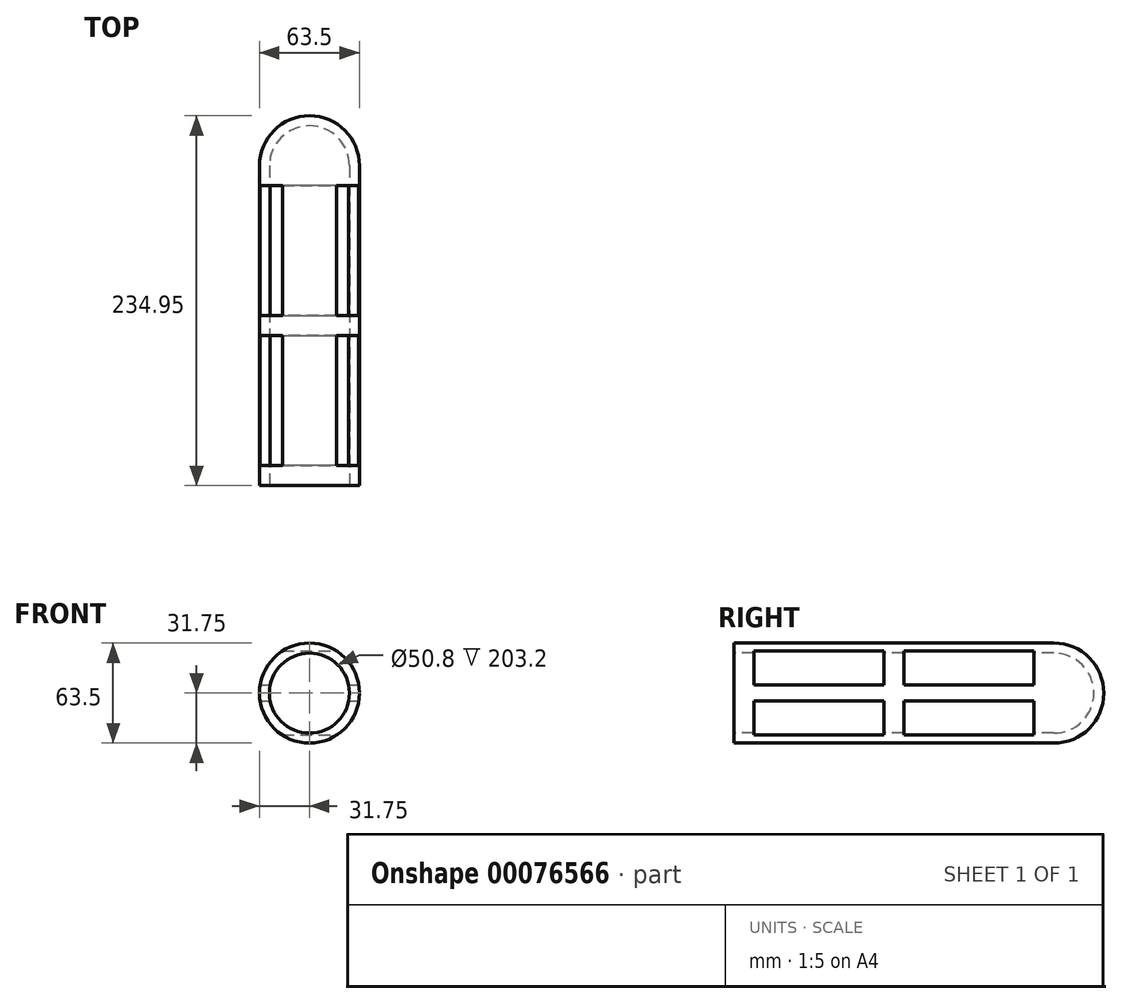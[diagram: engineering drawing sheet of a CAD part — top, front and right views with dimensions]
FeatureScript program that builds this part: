
annotation { "Feature Type Name" : "Feature", "Feature Type Description" : "" }
export const myFeature = defineFeature(function(context is Context, id is Id, definition is map)
    precondition{}
    {
        {
            var Q0;
            Q0=qCreatedBy(makeId("Front.planeOp"),FACE);
            var sketch = newSketch(context, id + "F0", { "sketchPlane" : qUnion([Q0])});
            skCircle(sketch, "E0", {"center": v(0, 0) * mm, "radius": 31.75 * mm});
            skCircle(sketch, "E1", {"center": v(0, 0) * mm, "radius": 25.4 * mm});
            skSolve(sketch);
        }
        {
            var Q0;
            Q0=makeQuery(id+"F0.imprint","IMPRINT",FACE,{"disambiguationData":[TD([[makeQuery(id+"F0.imprint","IMPRINT",EDGE,{"derivedFrom":sQuery(id+"F0.wireOp",EDGE,"E0")}),1.0]])]});
            extrude(context, id + "F1", {"entities" : qUnion([Q0]), "oppositeDirection" : true, "depth" : 203.2 * mm});
        }
        {
            var Q0;
            Q0=makeQuery(id+"F1.opExtrude","CAP_FACE",FACE,{"disambiguationData":[OSD([sQuery(id+"F0.wireOp",EDGE,"E0"),sQuery(id+"F0.wireOp",EDGE,"E1")])],"isStart":false});
            var sketch = newSketch(context, id + "F2", { "sketchPlane" : qUnion([Q0])});
            skLineSegment(sketch, "E2", {"start": v(0, 31.75) * mm, "end": v(0, -31.75) * mm, "construction": true});
            skArc(sketch, "E3", {"start": v(0, 31.75) * mm, "mid": v(-31.75, 0) * mm, "end": v(0, -31.75) * mm});
            skArc(sketch, "E4", {"start": v(0, 25.4) * mm, "mid": v(-25.4, 0) * mm, "end": v(0, -25.4) * mm});
            skLineSegment(sketch, "E5", {"start": v(0, 31.75) * mm, "end": v(0, 25.4) * mm});
            skLineSegment(sketch, "E6", {"start": v(0, -25.4) * mm, "end": v(0, -31.75) * mm});
            skSolve(sketch);
        }
        {
            var Q0;
            Q0=makeQuery(id+"F2.imprint","IMPRINT",FACE,{"disambiguationData":[TD([[makeQuery(id+"F2.imprint","IMPRINT",EDGE,{"derivedFrom":sQuery(id+"F2.wireOp",EDGE,"E3")}),-1.0]])]});
            var Q1;
            Q1=sQuery(id+"F2.wireOp",EDGE,"E2");
            revolve(context, id + "F3", {"operationType" : NewBodyOperationType.ADD, "entities" : qUnion([Q0]), "axis" : qUnion([Q1]), "revolveType" : RevolveType.ONE_DIRECTION, "oppositeDirection" : true, "angle" : 180 * degree});
        }
        {
            var Q0;
            Q0=qCreatedBy(makeId("Right.planeOp"),FACE);
            var sketch = newSketch(context, id + "F4", { "sketchPlane" : qUnion([Q0])});
            skLineSegment(sketch, "E7.bottom", {"start": v(190.5, 26.67) * mm, "end": v(12.7, 26.67) * mm});
            skLineSegment(sketch, "E7.top", {"start": v(190.5, 5.08) * mm, "end": v(12.7, 5.08) * mm});
            skLineSegment(sketch, "E7.left", {"start": v(190.5, 26.67) * mm, "end": v(190.5, 5.08) * mm});
            skLineSegment(sketch, "E7.right", {"start": v(12.7, 26.67) * mm, "end": v(12.7, 5.08) * mm});
            skLineSegment(sketch, "E8.0", {"start": v(0, -31.75) * mm, "end": v(0, 31.75) * mm});
            skLineSegment(sketch, "E9.MirrorCS", {"start": v(12.7, -26.67) * mm, "end": v(12.7, -5.08) * mm});
            skLineSegment(sketch, "E10.MirrorCS", {"start": v(190.5, -5.08) * mm, "end": v(12.7, -5.08) * mm});
            skLineSegment(sketch, "E11.MirrorCS", {"start": v(190.5, -26.67) * mm, "end": v(12.7, -26.67) * mm});
            skLineSegment(sketch, "E12.MirrorCS", {"start": v(190.5, -26.67) * mm, "end": v(190.5, -5.08) * mm});
            skLineSegment(sketch, "E13.top", {"start": v(101.6, -26.67) * mm, "end": v(101.6, -26.67) * mm});
            skLineSegment(sketch, "E14.bottom", {"start": v(133.19, 26.67) * mm, "end": v(120.59, 26.67) * mm});
            skLineSegment(sketch, "E14.top", {"start": v(133.29, 5.08) * mm, "end": v(120.59, 5.08) * mm});
            skLineSegment(sketch, "E15", {"start": v(101.6, 26.67) * mm, "end": v(101.6, -26.67) * mm, "construction": true});
            skLineSegment(sketch, "E16", {"start": v(107.95, 26.67) * mm, "end": v(107.95, -26.67) * mm});
            skLineSegment(sketch, "E17", {"start": v(95.25, 26.67) * mm, "end": v(95.25, -26.67) * mm});
            skSolve(sketch);
        }
        {
            var Q0;
            {var subQ7=sQuery(id+"F4.wireOp",EDGE,"E7.left");Q0=makeQuery(id+"F4.imprint","IMPRINT",FACE,{"disambiguationData":[TD([[makeQuery(id+"F4.imprint","IMPRINT",EDGE,{"derivedFrom":subQ7}),-1.0]])]});}
            var Q1;
            {var subQ0=sQuery(id+"F4.wireOp",EDGE,"E12.MirrorCS");Q1=makeQuery(id+"F4.imprint","IMPRINT",FACE,{"disambiguationData":[TD([[makeQuery(id+"F4.imprint","IMPRINT",EDGE,{"derivedFrom":subQ0}),1.0]])]});}
            var Q2;
            {var subQ0=sQuery(id+"F4.wireOp",EDGE,"E7.right");Q2=makeQuery(id+"F4.imprint","IMPRINT",FACE,{"disambiguationData":[TD([[makeQuery(id+"F4.imprint","IMPRINT",EDGE,{"derivedFrom":subQ0}),1.0]])]});}
            var Q3;
            {var subQ0=sQuery(id+"F4.wireOp",EDGE,"E9.MirrorCS");Q3=makeQuery(id+"F4.imprint","IMPRINT",FACE,{"disambiguationData":[TD([[makeQuery(id+"F4.imprint","IMPRINT",EDGE,{"derivedFrom":subQ0}),-1.0]])]});}
            extrude(context, id + "F5", {"entities" : qUnion([Q0, Q1, Q2, Q3]), "operationType" : NewBodyOperationType.REMOVE, "endBound" : BoundingType.SYMMETRIC, "oppositeDirection" : true, "depth" : 127 * mm});
        }
    });
